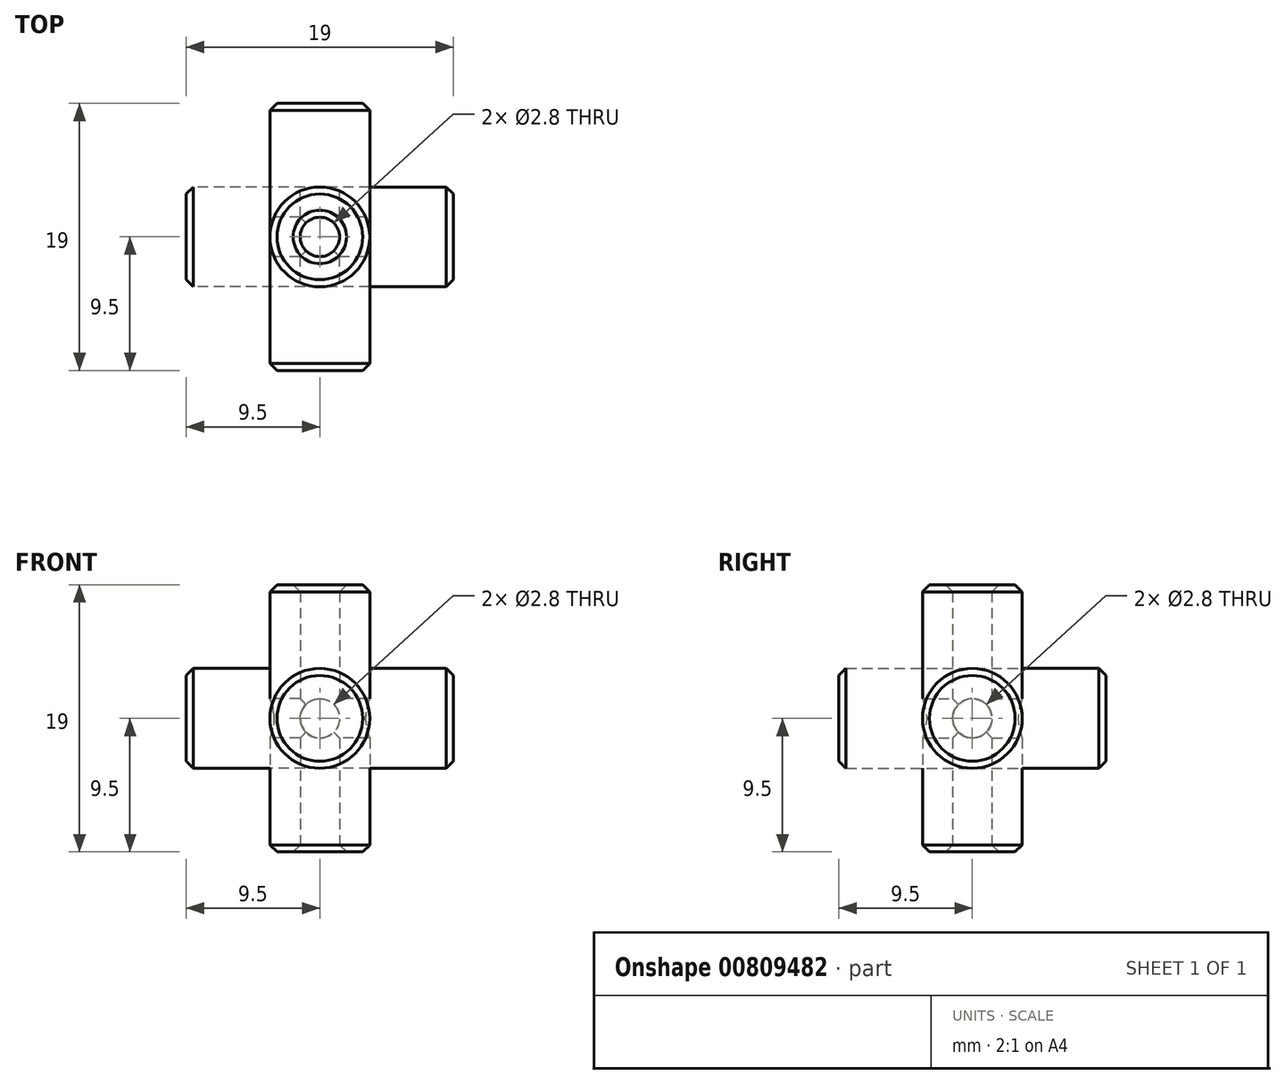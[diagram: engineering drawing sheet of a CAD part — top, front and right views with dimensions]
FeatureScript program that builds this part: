
annotation { "Feature Type Name" : "Feature", "Feature Type Description" : "" }
export const myFeature = defineFeature(function(context is Context, id is Id, definition is map)
    precondition{}
    {
        {
            var Q0;
            Q0=qCreatedBy(makeId("Front.planeOp"),FACE);
            var sketch = newSketch(context, id + "F0", { "sketchPlane" : qUnion([Q0])});
            skCircle(sketch, "E0", {"center": v(0, 0) * mm, "radius": 3.55 * mm});
            skSolve(sketch);
        }
        {
            var Q0;
            Q0 = qSketchRegion(id + "F0", true);
            extrude(context, id + "F1", {"entities" : qUnion([Q0]), "endBound" : BoundingType.SYMMETRIC, "depth" : 19 * mm, "offsetDistance" : 25 * mm});
        }
        {
            var Q0;
            Q0=qCreatedBy(makeId("Front.planeOp"),FACE);
            var sketch = newSketch(context, id + "F2", { "sketchPlane" : qUnion([Q0])});
            skCircle(sketch, "E1", {"center": v(0, 0) * mm, "radius": 1.4 * mm});
            skSolve(sketch);
        }
        {
            var Q0;
            Q0 = qSketchRegion(id + "F2", true);
            extrude(context, id + "F3", {"entities" : qUnion([Q0]), "endBound" : BoundingType.SYMMETRIC, "depth" : 20 * mm, "offsetDistance" : 25 * mm});
        }
        {
            var Q0;
            Q0=qCreatedBy(makeId("Front.planeOp"),FACE);
            var sketch = newSketch(context, id + "F4", { "sketchPlane" : qUnion([Q0])});
            skLineSegment(sketch, "E2.bottom", {"start": v(0, 0) * mm, "end": v(10, 0) * mm});
            skLineSegment(sketch, "E2.top", {"start": v(0, 10) * mm, "end": v(10, 10) * mm});
            skLineSegment(sketch, "E2.left", {"start": v(0, 0) * mm, "end": v(0, 10) * mm});
            skLineSegment(sketch, "E2.right", {"start": v(10, 0) * mm, "end": v(10, 10) * mm});
            skSolve(sketch);
        }
        {
            var Q0;
            Q0 = qSketchRegion(id + "F4", true);
            extrude(context, id + "F5", {"entities" : qUnion([Q0]), "depth" : 10 * mm, "offsetDistance" : 25 * mm});
        }
        {
            var Q0;
            Q0=qCreatedBy(makeId("Origin.pointOp"),VERTEX);
            var Q1;
            Q1=makeQuery(id+"F5.opExtrude","CAP_VERTEX",VERTEX,{"disambiguationData":[OSD([sQuery(id+"F4.wireOp",EDGE,"E2.top"),sQuery(id+"F4.wireOp",EDGE,"E2.right")])],"isStart":false});
            var Q2;
            Q2=makeQuery(id+"F5.opExtrude","CAP_VERTEX",VERTEX,{"disambiguationData":[OSD([sQuery(id+"F4.wireOp",EDGE,"E2.bottom"),sQuery(id+"F4.wireOp",EDGE,"E2.right")])],"isStart":false});
            cPlane(context, id + "F6", {"entities" : qUnion([Q0, Q1, Q2]), "cplaneType" : CPlaneType.THREE_POINT, "offset" : 25 * mm, "width" : 150 * mm, "height" : 150 * mm});
        }
        {
            var Q0;
            Q0=qCreatedBy(id+"F6.planeOp",FACE);
            var sketch = newSketch(context, id + "F7", { "sketchPlane" : qUnion([Q0])});
            skLineSegment(sketch, "E3", {"start": v(0, 0) * mm, "end": v(14.14, 10) * mm});
            skSolve(sketch);
        }
        {
            var Q0;
            Q0=makeQuery(id+"F5.opExtrude","SWEPT_BODY",BODY,{"disambiguationData":[OSD([sQuery(id+"F4.wireOp",EDGE,"E2.bottom"),sQuery(id+"F4.wireOp",EDGE,"E2.top"),sQuery(id+"F4.wireOp",EDGE,"E2.left"),sQuery(id+"F4.wireOp",EDGE,"E2.right")])]});
            deleteBodies(context, id + "F8", {"entities" : qUnion([Q0])});
        }
        {
            var Q0;
            Q0=makeQuery(id+"F3.opExtrude","SWEPT_BODY",BODY,{"disambiguationData":[OSD([sQuery(id+"F2.wireOp",EDGE,"E1")])]});
            var Q1;
            Q1=makeQuery(id+"F1.opExtrude","SWEPT_BODY",BODY,{"disambiguationData":[OSD([sQuery(id+"F0.wireOp",EDGE,"E0")])]});
            var Q2;
            Q2=sQuery(id+"F7.wireOp",EDGE,"E3");
            circularPattern(context, id + "F9", {"entities" : qUnion([Q0, Q1]), "axis" : qUnion([Q2]), "angle" : 360 * degree, "instanceCount" : 3, "equalSpace" : true});
        }
        {
            var Q0;
            Q0=makeQuery(id+"F9.opPattern","COPY",BODY,{"derivedFrom":makeQuery(id+"F3.opExtrude","SWEPT_BODY",BODY,{"disambiguationData":[OSD([sQuery(id+"F2.wireOp",EDGE,"E1")])]}),"instanceName":"2"});
            var Q1;
            Q1=makeQuery(id+"F9.opPattern","COPY",BODY,{"derivedFrom":makeQuery(id+"F3.opExtrude","SWEPT_BODY",BODY,{"disambiguationData":[OSD([sQuery(id+"F2.wireOp",EDGE,"E1")])]}),"instanceName":"1"});
            var Q2;
            Q2=makeQuery(id+"F3.opExtrude","SWEPT_BODY",BODY,{"disambiguationData":[OSD([sQuery(id+"F2.wireOp",EDGE,"E1")])]});
            var Q3;
            Q3=makeQuery(id+"F9.opPattern","COPY",BODY,{"derivedFrom":makeQuery(id+"F1.opExtrude","SWEPT_BODY",BODY,{"disambiguationData":[OSD([sQuery(id+"F0.wireOp",EDGE,"E0")])]}),"instanceName":"2"});
            booleanBodies(context, id + "F10", {"operationType" : BooleanOperationType.SUBTRACTION, "tools" : qUnion([Q0, Q1, Q2]), "targets" : qUnion([Q3])});
        }
        {
            var Q0;
            Q0=makeQuery(id+"F9.opPattern","COPY",FACE,{"derivedFrom":makeQuery(id+"F1.opExtrude","CAP_FACE",FACE,{"disambiguationData":[OSD([sQuery(id+"F0.wireOp",EDGE,"E0")])],"isStart":false}),"instanceName":"2"});
            var Q1;
            Q1=makeQuery(id+"F1.opExtrude","CAP_FACE",FACE,{"disambiguationData":[OSD([sQuery(id+"F0.wireOp",EDGE,"E0")])],"isStart":true});
            var Q2;
            Q2=makeQuery(id+"F9.opPattern","COPY",FACE,{"derivedFrom":makeQuery(id+"F1.opExtrude","CAP_FACE",FACE,{"disambiguationData":[OSD([sQuery(id+"F0.wireOp",EDGE,"E0")])],"isStart":false}),"instanceName":"1"});
            var Q3;
            Q3=makeQuery(id+"F9.opPattern","COPY",FACE,{"derivedFrom":makeQuery(id+"F1.opExtrude","CAP_FACE",FACE,{"disambiguationData":[OSD([sQuery(id+"F0.wireOp",EDGE,"E0")])],"isStart":true}),"instanceName":"1"});
            var Q4;
            Q4=makeQuery(id+"F1.opExtrude","CAP_FACE",FACE,{"disambiguationData":[OSD([sQuery(id+"F0.wireOp",EDGE,"E0")])],"isStart":false});
            var Q5;
            Q5=makeQuery(id+"F9.opPattern","COPY",FACE,{"derivedFrom":makeQuery(id+"F1.opExtrude","CAP_FACE",FACE,{"disambiguationData":[OSD([sQuery(id+"F0.wireOp",EDGE,"E0")])],"isStart":true}),"instanceName":"2"});
            chamfer(context, id + "F11", {"entities" : qUnion([Q0, Q1, Q2, Q3, Q4, Q5]), "width" : 0.5 * mm, "tangentPropagation" : true});
        }
    });
